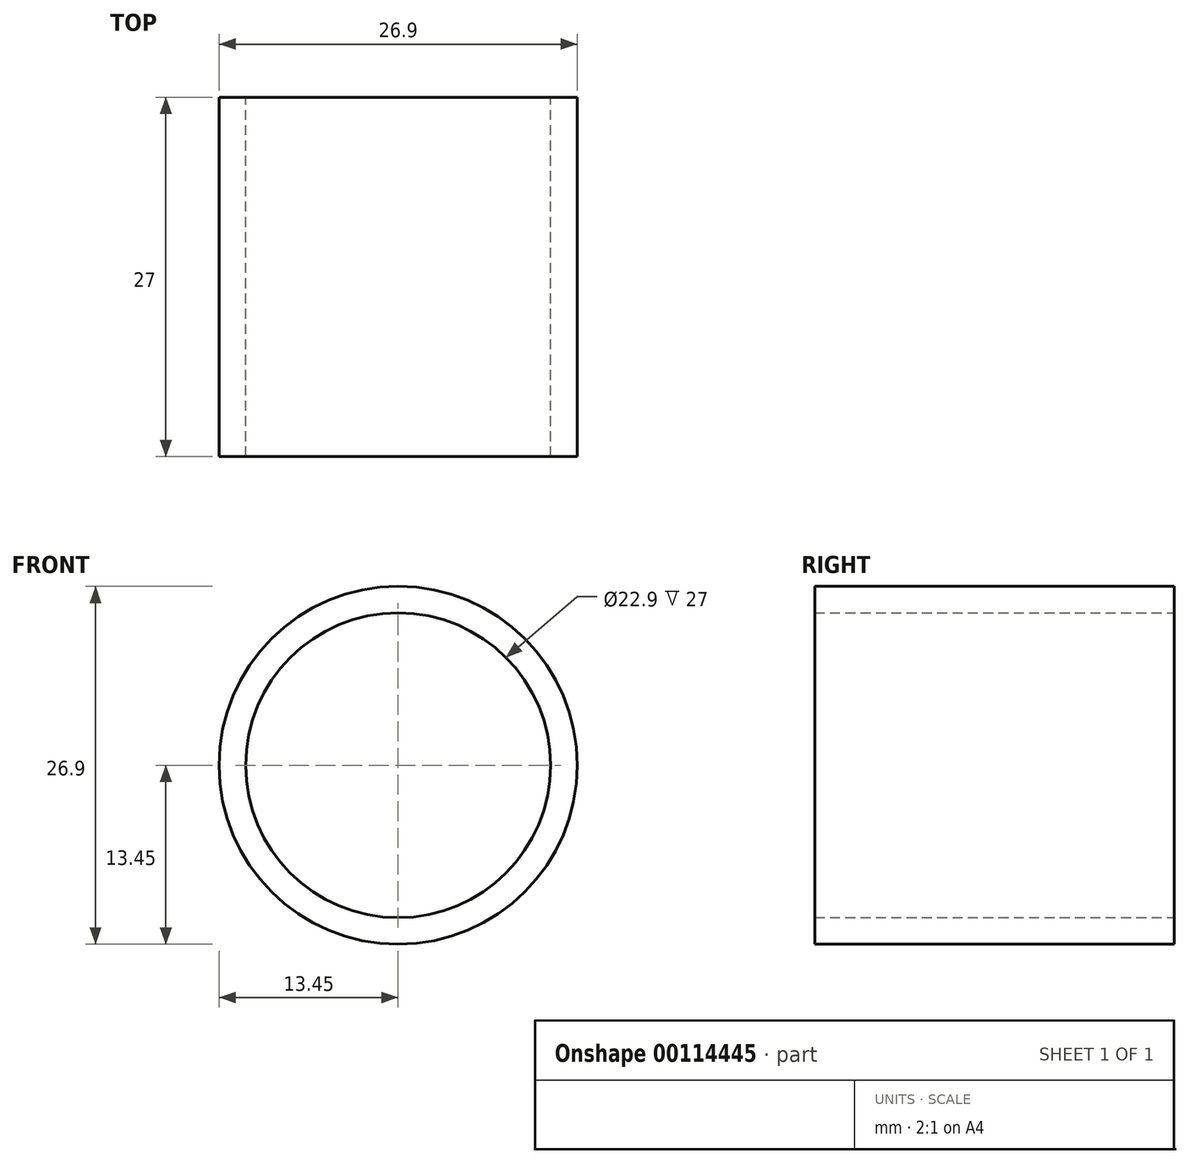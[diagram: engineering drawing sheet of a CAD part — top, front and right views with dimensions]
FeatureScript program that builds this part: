
annotation { "Feature Type Name" : "Feature", "Feature Type Description" : "" }
export const myFeature = defineFeature(function(context is Context, id is Id, definition is map)
    precondition{}
    {
        {
            var Q0;
            Q0=qCreatedBy(makeId("Front.planeOp"),FACE);
            var sketch = newSketch(context, id + "F0", { "sketchPlane" : qUnion([Q0])});
            skCircle(sketch, "E0", {"center": v(0, 0) * mm, "radius": 13.45 * mm});
            skCircle(sketch, "E1.0", {"center": v(0, 0) * mm, "radius": 11.45 * mm});
            skSolve(sketch);
        }
        {
            var Q0;
            Q0 = qSketchRegion(id + "F0", true);
            extrude(context, id + "F1", {"entities" : qUnion([Q0]), "depth" : 27 * mm});
        }
    });
